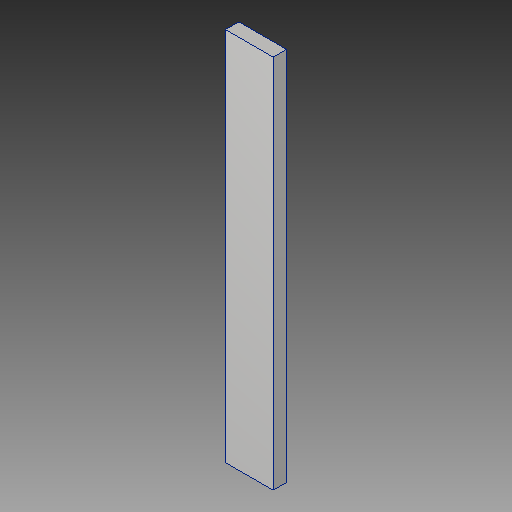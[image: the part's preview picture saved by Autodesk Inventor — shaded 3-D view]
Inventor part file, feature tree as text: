
AUTODESK INVENTOR PART (.ipt)
format: ipt  version: 2019 (Build 230136000, 136)  size: 94,720 bytes
history: native  units: in
note: dims shown in document units (in); Inventor stores cm internally (conversion verified against a paired STEP export)
features: extrude x1, sketch x1
ambient origin geometry x8: Origin, YZ Plane, XZ Plane, XY Plane, X Axis, Y Axis, Z Axis, Center Point
bodies: Solid1 (feature_tree)
feature tree (2):
  extrude  "Extrusion1"  Depth=14.0in
  sketch  "Sketch1"  dims[d0=1.78in d1=14.0in d2=0.5in d3=0.0in]
